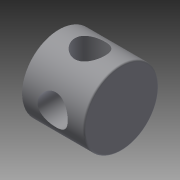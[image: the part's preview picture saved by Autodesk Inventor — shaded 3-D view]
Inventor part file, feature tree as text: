
AUTODESK INVENTOR PART (.ipt)
format: ipt  version: 2015 SP1 (Build 190203100, 203)  size: 134,144 bytes
history: native  units: in
note: dims shown in document units (in); Inventor stores cm internally (conversion verified against a paired STEP export)
features: fillet x1, other x1, imported_body x1
ambient origin geometry x8: Origin, YZ Plane, XZ Plane, XY Plane, X Axis, Y Axis, Z Axis, Center Point
bodies: Body1 (feature_tree)
feature tree (3):
  fillet  "Fillet2"  [1 undecoded]
  other  "276-2045-002-002 Rev2.ipt1"
  imported_body  "Base1"
note: 1 required parameter value undecoded (feature->parameter linkage not recoverable at this tier; creation-order binding heuristic only, values carry confidence <= 0.55)
